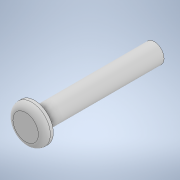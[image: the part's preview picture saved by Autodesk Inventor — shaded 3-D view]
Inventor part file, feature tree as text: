
AUTODESK INVENTOR PART (.ipt)
format: ipt  version: 2021 (Build 250183000, 183)  size: 122,880 bytes
history: native  units: in
note: dims shown in document units (in); Inventor stores cm internally (conversion verified against a paired STEP export)
features: revolve x1, fillet x1, sketch x1
ambient origin geometry x8: Origin, YZ Plane, XZ Plane, XY Plane, X Axis, Y Axis, Z Axis, Center Point
bodies: Solid1 (feature_tree)
feature tree (3):
  revolve  "Revolution1"  [1 undecoded]
  fillet  "Fillet1"  Radius=0.0492in
  sketch  "Sketch2"  dims[d0=0.0256in d1=0.1575in d2=0.0492in d3=0.0118in d4=90.0deg d5=0.0079in]
note: 1 required parameter value undecoded (feature->parameter linkage not recoverable at this tier; creation-order binding heuristic only, values carry confidence <= 0.55)
